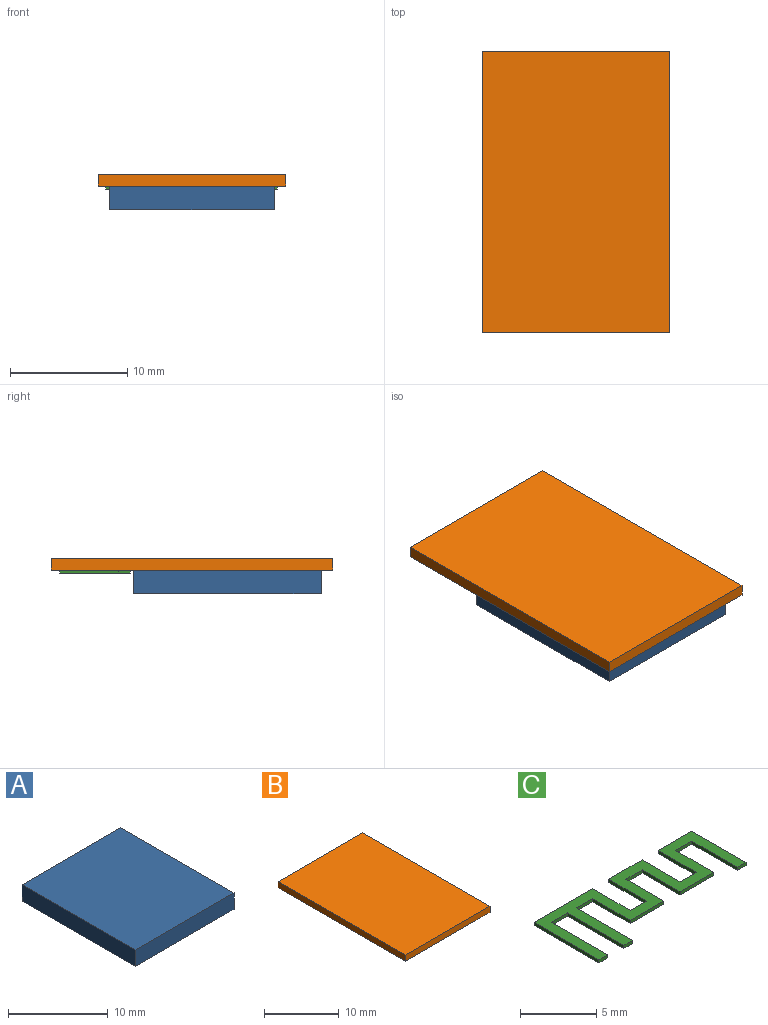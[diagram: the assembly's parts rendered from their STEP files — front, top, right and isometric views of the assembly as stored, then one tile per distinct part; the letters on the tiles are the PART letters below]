
ASSEMBLY  parts=3 mates=2
PART A: 6 faces, bbox 14x16x2 mm
  f0: plane 16x2mm, normal (-1,0,0), area 32mm2, adj f1,f3,f4,f5
  f1: plane 14x2mm, normal (0,-1,0), area 28mm2, adj f0,f2,f4,f5
  f2: plane 16x2mm, normal (1,0,0), area 32mm2, adj f1,f3,f4,f5
  f3: plane 14x2mm, normal (0,1,0), area 28mm2, adj f0,f2,f4,f5
  f4: plane 16x14mm, normal (0,0,1), area 224mm2, adj f0,f1,f2,f3
  f5: plane 16x14mm, normal (0,0,-1), area 224mm2, adj f0,f1,f2,f3
PART B: 6 faces, bbox 16x24x1 mm
  f0: plane 24x1mm, normal (-1,0,0), area 24mm2, adj f1,f3,f4,f5
  f1: plane 16x1mm, normal (0,-1,0), area 16mm2, adj f0,f2,f4,f5
  f2: plane 24x1mm, normal (1,0,0), area 24mm2, adj f1,f3,f4,f5
  f3: plane 16x1mm, normal (0,1,0), area 16mm2, adj f0,f2,f4,f5
  f4: plane 24x16mm, normal (0,0,1), area 384mm2, adj f0,f1,f2,f3
  f5: plane 24x16mm, normal (0,0,-1), area 384mm2, adj f0,f1,f2,f3
PART C: 30 faces, bbox 14.6x6x0.3 mm
  f0: plane 5.4x0.25mm, normal (0,1,0), area 1.4mm2, adj f1,f27,f28,f29
  f1: plane 6x0.25mm, normal (-1,0,0), area 1.5mm2, adj f0,f2,f28,f29
  f2: plane 0.8x0.25mm, normal (0,-1,0), area 0.2mm2, adj f1,f3,f28,f29
  f3: plane 5.2x0.25mm, normal (1,0,0), area 1.3mm2, adj f2,f4,f28,f29
  f4: plane 1.5x0.25mm, normal (0,-1,0), area 0.4mm2, adj f3,f5,f28,f29
  f5: plane 5.2x0.25mm, normal (-1,0,0), area 1.3mm2, adj f4,f6,f28,f29
  f6: plane 0.8x0.25mm, normal (0,-1,0), area 0.2mm2, adj f5,f7,f28,f29
  f7: plane 5.2x0.25mm, normal (1,0,0), area 1.3mm2, adj f6,f8,f28,f29
  f8: plane 1.5x0.25mm, normal (0,-1,0), area 0.4mm2, adj f7,f9,f28,f29
  f9: plane 3.5x0.25mm, normal (-1,0,0), area 0.9mm2, adj f8,f10,f28,f29
  f10: plane 3.1x0.25mm, normal (0,-1,0), area 0.8mm2, adj f9,f11,f28,f29
  f11: plane 3.5x0.25mm, normal (1,0,0), area 0.9mm2, adj f10,f12,f28,f29
  f12: plane 1.5x0.25mm, normal (0,-1,0), area 0.4mm2, adj f11,f13,f28,f29
  f13: plane 3.5x0.25mm, normal (-1,0,0), area 0.9mm2, adj f12,f14,f28,f29
  f14: plane 3.1x0.25mm, normal (0,-1,0), area 0.8mm2, adj f13,f15,f28,f29
  f15: plane 3.5x0.25mm, normal (1,0,0), area 0.9mm2, adj f14,f16,f28,f29
  f16: plane 1.5x0.25mm, normal (0,-1,0), area 0.4mm2, adj f15,f17,f28,f29
  f17: plane 4.2x0.25mm, normal (-1,0,0), area 1.1mm2, adj f16,f18,f28,f29
  f18: plane 0.8x0.25mm, normal (0,-1,0), area 0.2mm2, adj f17,f19,f28,f29
  f19: plane 5x0.25mm, normal (1,0,0), area 1.2mm2, adj f18,f20,f28,f29
  f20: plane 3.1x0.25mm, normal (0,1,0), area 0.8mm2, adj f19,f21,f28,f29
  f21: plane 3.5x0.25mm, normal (-1,0,0), area 0.9mm2, adj f20,f22,f28,f29
  f22: plane 1.5x0.25mm, normal (0,1,0), area 0.4mm2, adj f21,f23,f28,f29
  f23: plane 3.5x0.25mm, normal (1,0,0), area 0.9mm2, adj f22,f24,f28,f29
  f24: plane 3.1x0.25mm, normal (0,1,0), area 0.8mm2, adj f23,f25,f28,f29
  f25: plane 3.5x0.25mm, normal (-1,0,0), area 0.9mm2, adj f24,f26,f28,f29
  f26: plane 1.5x0.25mm, normal (0,1,0), area 0.4mm2, adj f25,f27,f28,f29
  f27: plane 3.5x0.25mm, normal (1,0,0), area 0.9mm2, adj f0,f26,f28,f29
  f28: plane 14.6x6mm, normal (0,0,1), area 34.6mm2, adj f0,f1,f2,f3,f4,f5,f6,f7
  f29: plane 14.6x6mm, normal (0,0,-1), area 34.6mm2, adj f0,f1,f2,f3,f4,f5,f6,f7
PLACE A t=(2.06,-3.99,0.17)mm
PLACE B t=(1.06,-4.99,2.17)mm fixed
PLACE C rot(axis=(0,1,0),180deg) t=(44.67,2.71,2.17)mm
MATE fastened C.f29 <-> B.f5  axis (0,0,1) through (16.31,18.26,2.17)mm
MATE fastened A.f4 <-> B.f5  axis (0,0,1) through (16.06,-3.99,2.17)mm
